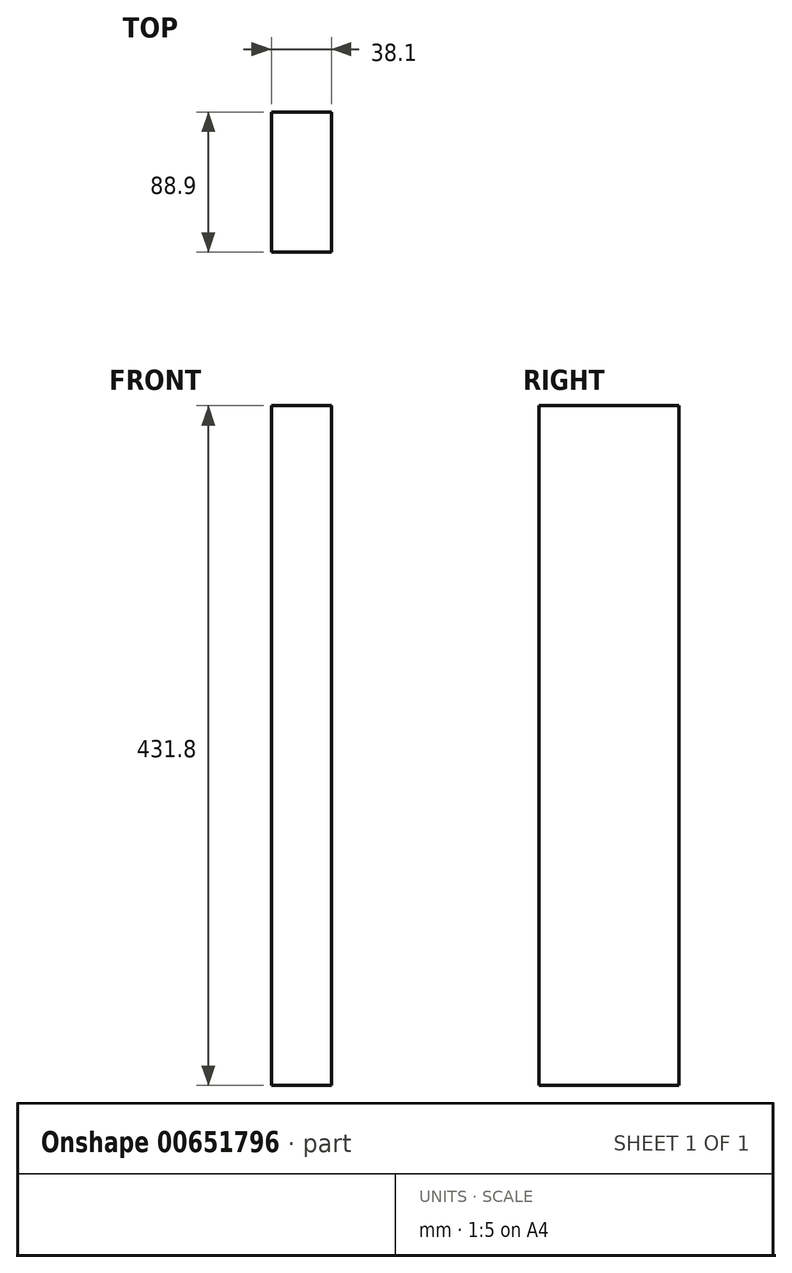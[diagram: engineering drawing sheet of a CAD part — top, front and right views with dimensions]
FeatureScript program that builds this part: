
annotation { "Feature Type Name" : "Feature", "Feature Type Description" : "" }
export const myFeature = defineFeature(function(context is Context, id is Id, definition is map)
    precondition{}
    {
        {
            var Q0;
            Q0=qCreatedBy(makeId("Top.planeOp"),FACE);
            var sketch = newSketch(context, id + "F0", { "sketchPlane" : qUnion([Q0])});
            skLineSegment(sketch, "E0.bottom", {"start": v(0, 0) * mm, "end": v(38.1, 0) * mm});
            skLineSegment(sketch, "E0.top", {"start": v(0, 88.9) * mm, "end": v(38.1, 88.9) * mm});
            skLineSegment(sketch, "E0.left", {"start": v(0, 0) * mm, "end": v(0, 88.9) * mm});
            skLineSegment(sketch, "E0.right", {"start": v(38.1, 0) * mm, "end": v(38.1, 88.9) * mm});
            skSolve(sketch);
        }
        {
            var Q0;
            Q0=makeQuery(id+"F0.imprint","IMPRINT",FACE,{"disambiguationData":[TD([[makeQuery(id+"F0.imprint","IMPRINT",EDGE,{"derivedFrom":sQuery(id+"F0.wireOp",EDGE,"E0.bottom")}),1.0]])]});
            extrude(context, id + "F1", {"entities" : qUnion([Q0]), "depth" : 431.8 * mm, "offsetDistance" : 25.4 * mm});
        }
    });
